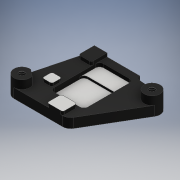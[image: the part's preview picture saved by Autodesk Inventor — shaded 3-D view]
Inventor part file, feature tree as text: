
AUTODESK INVENTOR PART (.ipt)
format: ipt  version: 2018 (Build 220112000, 112)  size: 267,264 bytes
history: native  units: mm
features: extrude x7, sketch x3, projected_geometry x3, hole x2
ambient origin geometry x8: Origin, YZ Plane, XZ Plane, XY Plane, X Axis, Y Axis, Z Axis, Center Point
bodies: Body1 (feature_tree)
feature tree (15):
  sketch  "Sketch9"  dims[d71=4.0mm d72=19.9mm]
  extrude  "Extrusion7"  Depth=4.0mm
  hole  "Hole3"  [1 undecoded]
  extrude  "Extrusion8"  Depth=3.0mm
  extrude  "Extrusion9"  Depth=3.0mm
  extrude  "Extrusion10"  Depth=2.15mm
  extrude  "Extrusion11"  Depth=1.9mm
  extrude  "Extrusion12"  Depth=3.0mm
  extrude  "Extrusion13"  Depth=3.0mm
  hole  "Hole4"  [1 undecoded]
  sketch  "Sketch10"  dims[d73=12.9mm d74=9.3mm]
  projected_geometry  "Projected Loop10"
  projected_geometry  "Projected Loop11"
  sketch  "Sketch11"  dims[d75=6.3mm d76=7.5mm d77=5.9mm d78=2.15mm d79=1.9mm d80=1.95mm d81=6.5mm d82=1.0mm d83=3.15mm d84=3.5mm d85=1.0mm d86=0.0mm d87=0.0mm d88=1.567mm d89=4.0mm d90=4.0mm d91=2.0mm d92=90.0deg d93=6.3mm d94=20.594885mm d95=2.0mm d96=3.0mm d97=10.1mm d101=3.5mm d102=0.0mm d103=1.0mm d104=8.5mm d105=0.5mm d106=0.0mm d107=6.4mm d108=2.8mm d109=4.0mm d110=0.3mm d111=1.8mm d112=1.4mm d113=0.0mm d114=0.5mm d115=0.5mm d116=4.0mm d117=2.5mm d118=2.5mm d119=2.1mm d120=1.710742mm d121=2.27mm d122=0.0mm d123=2.15mm d124=0.0mm d125=1.0mm d127=1.0mm d128=4.0mm d129=3.2mm d130=4.0mm d131=2.3mm d132=0.0mm d133=1.221mm d134=3.2mm d135=4.0mm d136=2.0mm d137=90.0deg d138=3.0mm d139=20.594885mm]
  projected_geometry  "Projected Loop12"
note: 2 required parameter values undecoded (feature->parameter linkage not recoverable at this tier; creation-order binding heuristic only, values carry confidence <= 0.55)
